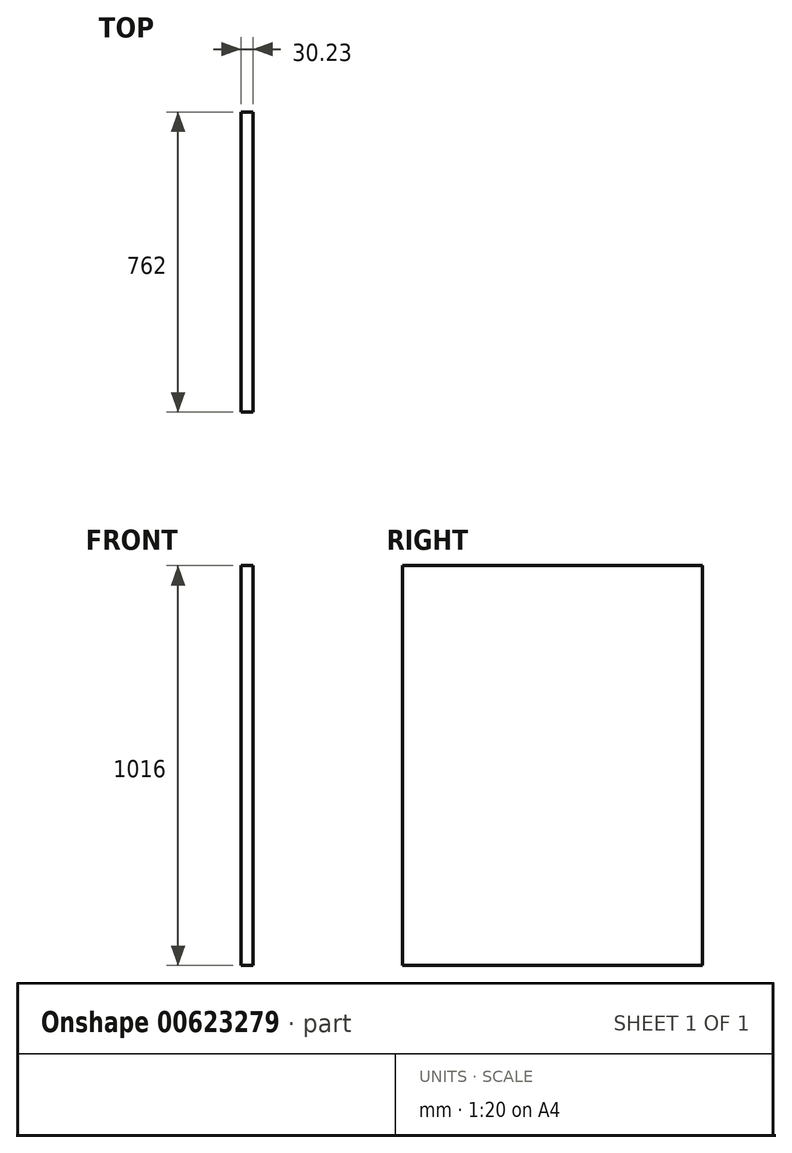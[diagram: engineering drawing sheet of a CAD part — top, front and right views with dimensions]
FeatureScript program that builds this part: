
annotation { "Feature Type Name" : "Feature", "Feature Type Description" : "" }
export const myFeature = defineFeature(function(context is Context, id is Id, definition is map)
    precondition{}
    {
        {
            var Q0;
            Q0=qCreatedBy(makeId("Right.planeOp"),FACE);
            var sketch = newSketch(context, id + "F0", { "sketchPlane" : qUnion([Q0])});
            skLineSegment(sketch, "E0.bottom", {"start": v(381, 508) * mm, "end": v(-381, 508) * mm});
            skLineSegment(sketch, "E0.top", {"start": v(381, -508) * mm, "end": v(-381, -508) * mm});
            skLineSegment(sketch, "E0.left", {"start": v(381, 508) * mm, "end": v(381, -508) * mm});
            skLineSegment(sketch, "E0.right", {"start": v(-381, 508) * mm, "end": v(-381, -508) * mm});
            skPoint(sketch, "E0.middle", {"position": v(0, 0) * mm});
            skSolve(sketch);
        }
        {
            var Q0;
            Q0=makeQuery(id+"F0.imprint","IMPRINT",FACE,{"disambiguationData":[TD([[makeQuery(id+"F0.imprint","IMPRINT",EDGE,{"derivedFrom":sQuery(id+"F0.wireOp",EDGE,"E0.bottom")}),1.0]])]});
            extrude(context, id + "F1", {"entities" : qUnion([Q0]), "depth" : 30.23 * mm, "offsetDistance" : 25.4 * mm});
        }
    });
